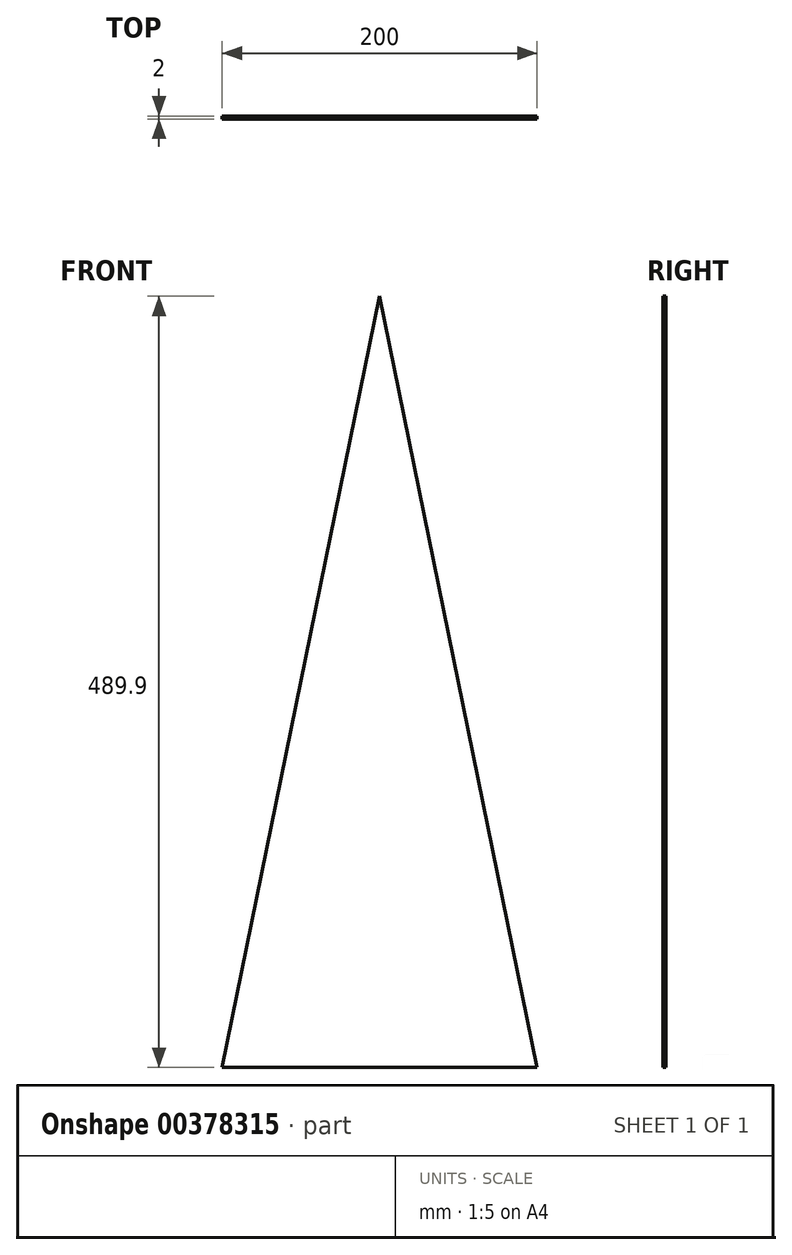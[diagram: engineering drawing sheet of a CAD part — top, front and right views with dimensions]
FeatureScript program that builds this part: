
annotation { "Feature Type Name" : "Feature", "Feature Type Description" : "" }
export const myFeature = defineFeature(function(context is Context, id is Id, definition is map)
    precondition{}
    {
        {
            var Q0;
            Q0=qCreatedBy(makeId("Front.planeOp"),FACE);
            var sketch = newSketch(context, id + "F0", { "sketchPlane" : qUnion([Q0])});
            skLineSegment(sketch, "E0", {"start": v(0, 0) * mm, "end": v(200, 0) * mm});
            skLineSegment(sketch, "E1", {"start": v(200, 0) * mm, "end": v(100, 489.9) * mm});
            skLineSegment(sketch, "E2", {"start": v(100, 489.9) * mm, "end": v(0, 0) * mm});
            skSolve(sketch);
        }
        {
            var Q0;
            Q0=makeQuery(id+"F0.imprint","IMPRINT",FACE,{"disambiguationData":[TD([[makeQuery(id+"F0.imprint","IMPRINT",EDGE,{"derivedFrom":sQuery(id+"F0.wireOp",EDGE,"E0")}),1.0]])]});
            extrude(context, id + "F1", {"entities" : qUnion([Q0]), "depth" : 2 * mm});
        }
    });
